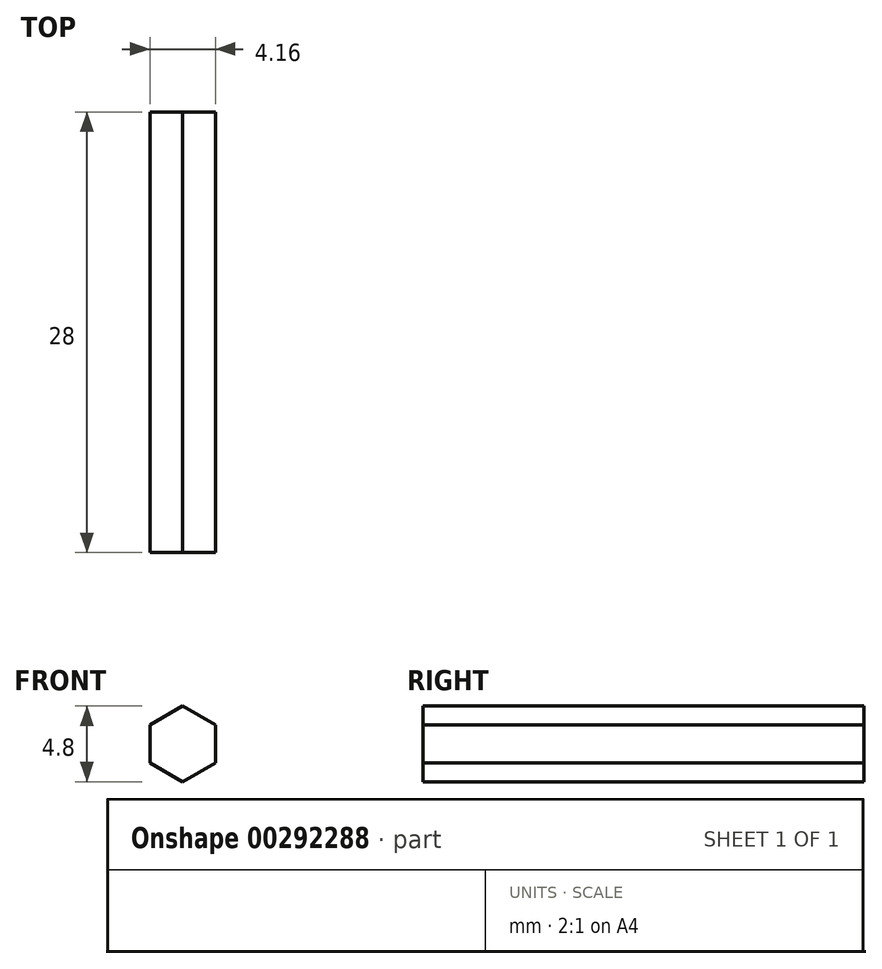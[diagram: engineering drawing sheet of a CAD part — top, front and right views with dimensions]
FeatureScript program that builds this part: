
annotation { "Feature Type Name" : "Feature", "Feature Type Description" : "" }
export const myFeature = defineFeature(function(context is Context, id is Id, definition is map)
    precondition{}
    {
        {
            var Q0;
            Q0=qCreatedBy(makeId("Front.planeOp"),FACE);
            var sketch = newSketch(context, id + "F0", { "sketchPlane" : qUnion([Q0])});
            skCircle(sketch, "E0.cCircle", {"center": v(0, 0) * mm, "radius": 2.4 * mm, "construction": true});
            skLineSegment(sketch, "E0.0", {"start": v(2.08, -1.2) * mm, "end": v(0, -2.4) * mm});
            skLineSegment(sketch, "E0.1", {"start": v(0, -2.4) * mm, "end": v(-2.08, -1.2) * mm});
            skLineSegment(sketch, "E0.2", {"start": v(-2.08, -1.2) * mm, "end": v(-2.08, 1.2) * mm});
            skLineSegment(sketch, "E0.3", {"start": v(-2.08, 1.2) * mm, "end": v(0, 2.4) * mm});
            skLineSegment(sketch, "E0.4", {"start": v(0, 2.4) * mm, "end": v(2.08, 1.2) * mm});
            skLineSegment(sketch, "E0.5", {"start": v(2.08, 1.2) * mm, "end": v(2.08, -1.2) * mm});
            skSolve(sketch);
        }
        {
            var Q0;
            Q0=makeQuery(id+"F0.imprint","IMPRINT",FACE,{"disambiguationData":[TD([[makeQuery(id+"F0.imprint","IMPRINT",EDGE,{"derivedFrom":sQuery(id+"F0.wireOp",EDGE,"E0.0")}),-1.0]])]});
            extrude(context, id + "F1", {"entities" : qUnion([Q0]), "depth" : 28 * mm});
        }
    });
